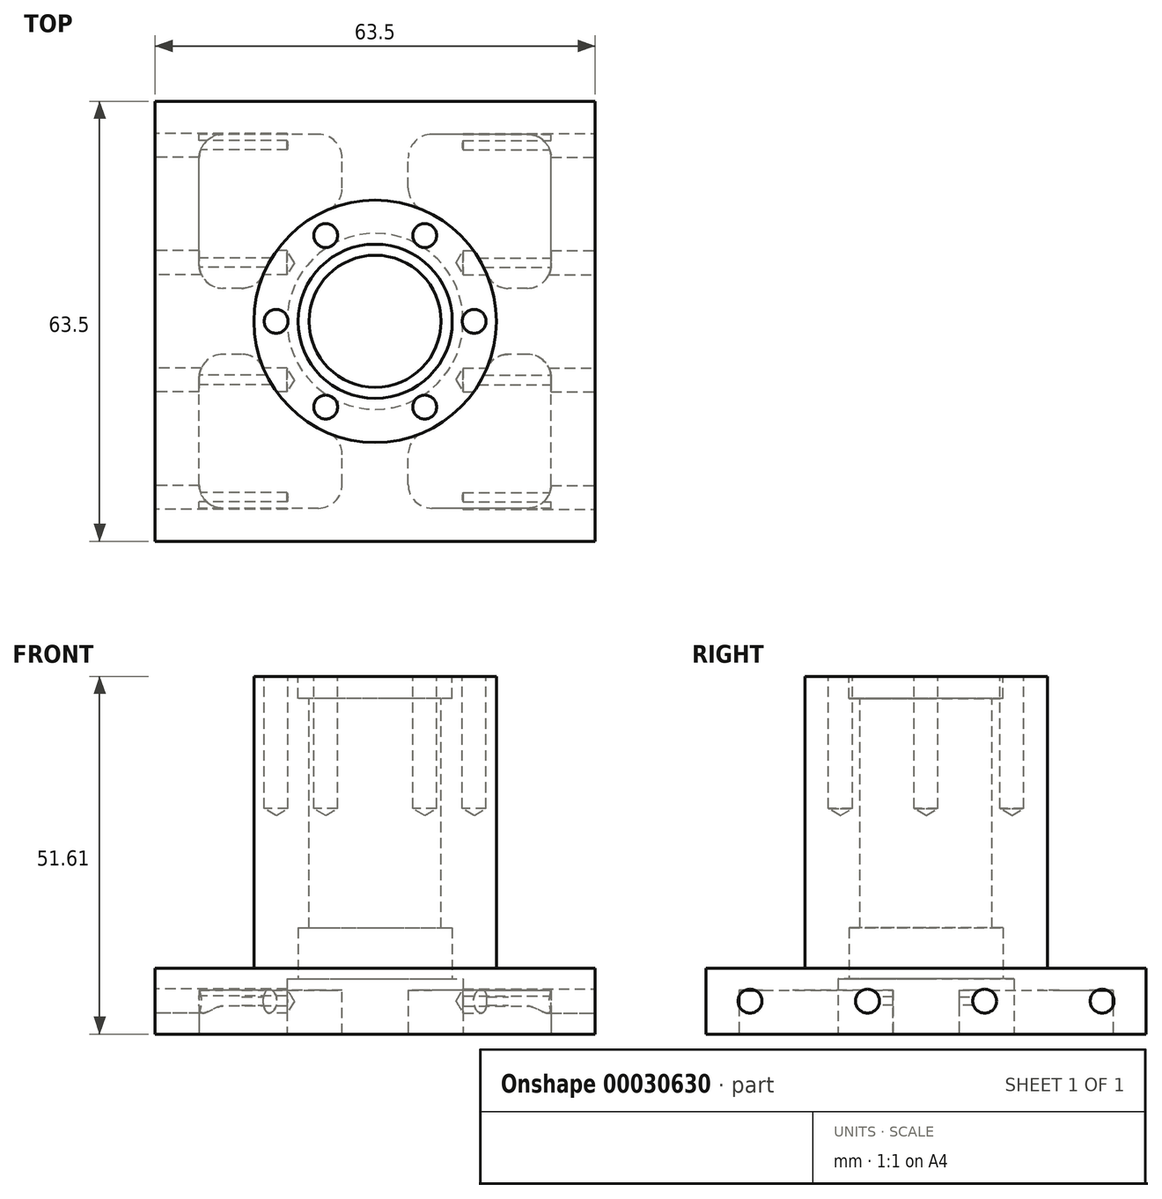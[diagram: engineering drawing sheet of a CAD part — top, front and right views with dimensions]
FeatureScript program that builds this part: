
annotation { "Feature Type Name" : "Feature", "Feature Type Description" : "" }
export const myFeature = defineFeature(function(context is Context, id is Id, definition is map)
    precondition{}
    {
        {
            var Q0;
            Q0=qCreatedBy(makeId("Top.planeOp"),FACE);
            var sketch = newSketch(context, id + "F0", { "sketchPlane" : qUnion([Q0])});
            skLineSegment(sketch, "E0.rect.bottom", {"start": v(31.75, -31.75) * mm, "end": v(-31.75, -31.75) * mm});
            skLineSegment(sketch, "E0.rect.top", {"start": v(31.75, 31.75) * mm, "end": v(-31.75, 31.75) * mm});
            skLineSegment(sketch, "E0.rect.left", {"start": v(31.75, -31.75) * mm, "end": v(31.75, 31.75) * mm});
            skLineSegment(sketch, "E0.rect.right", {"start": v(-31.75, -31.75) * mm, "end": v(-31.75, 31.75) * mm});
            skPoint(sketch, "E0.rect.middle", {"position": v(0, 0) * mm});
            skSolve(sketch);
        }
        {
            var Q0;
            Q0=makeQuery(id+"F0.imprint","IMPRINT",FACE,{"disambiguationData":[TD([[makeQuery(id+"F0.imprint","IMPRINT",EDGE,{"derivedFrom":sQuery(id+"F0.wireOp",EDGE,"E0.rect.bottom")}),-1.0]])]});
            extrude(context, id + "F1", {"entities" : qUnion([Q0]), "depth" : 9.52 * mm});
        }
        {
            var Q0;
            Q0=makeQuery(id+"F1.opExtrude","CAP_FACE",FACE,{"disambiguationData":[OSD([sQuery(id+"F0.wireOp",EDGE,"E0.rect.bottom"),sQuery(id+"F0.wireOp",EDGE,"E0.rect.top"),sQuery(id+"F0.wireOp",EDGE,"E0.rect.left"),sQuery(id+"F0.wireOp",EDGE,"E0.rect.right")])],"isStart":false});
            var sketch = newSketch(context, id + "F2", { "sketchPlane" : qUnion([Q0])});
            skCircle(sketch, "E1", {"center": v(0, 0) * mm, "radius": 17.49 * mm});
            skSolve(sketch);
        }
        {
            var Q0;
            Q0=makeQuery(id+"F2.imprint","IMPRINT",FACE,{"disambiguationData":[TD([[makeQuery(id+"F2.imprint","IMPRINT",EDGE,{"derivedFrom":sQuery(id+"F2.wireOp",EDGE,"E1")}),1.0]])]});
            extrude(context, id + "F3", {"entities" : qUnion([Q0]), "operationType" : NewBodyOperationType.ADD, "depth" : 42.1 * mm});
        }
        {
            var Q0;
            Q0=makeQuery(id+"F3.opExtrude","CAP_FACE",FACE,{"disambiguationData":[OSD([sQuery(id+"F2.wireOp",EDGE,"E1")])],"isStart":false});
            var sketch = newSketch(context, id + "F4", { "sketchPlane" : qUnion([Q0])});
            skCircle(sketch, "E2", {"center": v(0, 0) * mm, "radius": 9.53 * mm});
            skSolve(sketch);
        }
        {
            var Q0;
            Q0 = qSketchRegion(id + "F4", true);
            extrude(context, id + "F5", {"entities" : qUnion([Q0]), "operationType" : NewBodyOperationType.REMOVE, "endBound" : BoundingType.THROUGH_ALL, "oppositeDirection" : true, "depth" : 25.4 * mm});
        }
        {
            var Q0;
            Q0=makeQuery(id+"F3.opExtrude","CAP_FACE",FACE,{"disambiguationData":[OSD([sQuery(id+"F2.wireOp",EDGE,"E1")])],"isStart":false});
            var sketch = newSketch(context, id + "F6", { "sketchPlane" : qUnion([Q0])});
            skCircle(sketch, "E3", {"center": v(0, 0) * mm, "radius": 11.13 * mm});
            skSolve(sketch);
        }
        {
            var Q0;
            Q0=makeQuery(id+"F6.imprint","IMPRINT",FACE,{"disambiguationData":[TD([[makeQuery(id+"F6.imprint","IMPRINT",EDGE,{"derivedFrom":sQuery(id+"F6.wireOp",EDGE,"E3")}),1.0]])]});
            extrude(context, id + "F7", {"entities" : qUnion([Q0]), "operationType" : NewBodyOperationType.REMOVE, "oppositeDirection" : true, "depth" : 3.17 * mm});
        }
        {
            var Q0;
            Q0=makeQuery(id+"F1.opExtrude","CAP_FACE",FACE,{"disambiguationData":[OSD([sQuery(id+"F0.wireOp",EDGE,"E0.rect.bottom"),sQuery(id+"F0.wireOp",EDGE,"E0.rect.top"),sQuery(id+"F0.wireOp",EDGE,"E0.rect.left"),sQuery(id+"F0.wireOp",EDGE,"E0.rect.right")])],"isStart":true});
            var sketch = newSketch(context, id + "F8", { "sketchPlane" : qUnion([Q0])});
            skCircle(sketch, "E4", {"center": v(0, 0) * mm, "radius": 11.13 * mm});
            skSolve(sketch);
        }
        {
            var Q0;
            Q0 = qSketchRegion(id + "F8", true);
            extrude(context, id + "F9", {"entities" : qUnion([Q0]), "operationType" : NewBodyOperationType.REMOVE, "oppositeDirection" : true, "depth" : 15.32 * mm});
        }
        {
            var Q0;
            Q0=makeQuery(id+"F1.opExtrude","CAP_FACE",FACE,{"disambiguationData":[OSD([sQuery(id+"F0.wireOp",EDGE,"E0.rect.bottom"),sQuery(id+"F0.wireOp",EDGE,"E0.rect.top"),sQuery(id+"F0.wireOp",EDGE,"E0.rect.left"),sQuery(id+"F0.wireOp",EDGE,"E0.rect.right")])],"isStart":true});
            var sketch = newSketch(context, id + "F10", { "sketchPlane" : qUnion([Q0])});
            skCircle(sketch, "E5", {"center": v(0, 0) * mm, "radius": 12.7 * mm});
            skSolve(sketch);
        }
        {
            var Q0;
            Q0=makeQuery(id+"F10.imprint","IMPRINT",FACE,{"disambiguationData":[TD([[makeQuery(id+"F10.imprint","IMPRINT",EDGE,{"derivedFrom":sQuery(id+"F10.wireOp",EDGE,"E5")}),1.0]])]});
            var Q1;
            Q1=sQuery(id+"F10.wireOp",EDGE,"E5");
            extrude(context, id + "F11", {"entities" : qUnion([Q0]), "operationType" : NewBodyOperationType.REMOVE, "surfaceEntities" : qUnion([Q1]), "oppositeDirection" : true, "depth" : 7.95 * mm});
        }
        {
            var Q0;
            Q0=makeQuery(id+"F3.opExtrude","CAP_FACE",FACE,{"disambiguationData":[OSD([sQuery(id+"F2.wireOp",EDGE,"E1")])],"isStart":false});
            var sketch = newSketch(context, id + "F12", { "sketchPlane" : qUnion([Q0])});
            skCircle(sketch, "E6.cCircle", {"center": v(0, 0) * mm, "radius": 14.29 * mm, "construction": true});
            skLineSegment(sketch, "E6.0", {"start": v(-14.29, 0) * mm, "end": v(-7.14, 12.37) * mm});
            skLineSegment(sketch, "E6.1", {"start": v(-7.14, 12.37) * mm, "end": v(7.14, 12.37) * mm});
            skLineSegment(sketch, "E6.2", {"start": v(7.14, 12.37) * mm, "end": v(14.29, 0) * mm});
            skLineSegment(sketch, "E6.3", {"start": v(14.29, 0) * mm, "end": v(7.14, -12.37) * mm});
            skLineSegment(sketch, "E6.4", {"start": v(7.14, -12.37) * mm, "end": v(-7.14, -12.37) * mm});
            skLineSegment(sketch, "E6.5", {"start": v(-7.14, -12.37) * mm, "end": v(-14.29, 0) * mm});
            skSolve(sketch);
        }
        {
            var Q0;
            Q0=sQuery(id+"F12.wireOp",VERTEX,"E6.3.start");
            var Q1;
            Q1=sQuery(id+"F12.wireOp",VERTEX,"E6.4.start");
            var Q2;
            Q2=sQuery(id+"F12.wireOp",VERTEX,"E6.5.start");
            var Q3;
            Q3=sQuery(id+"F12.wireOp",VERTEX,"E6.5.end");
            var Q4;
            Q4=sQuery(id+"F12.wireOp",VERTEX,"E6.1.start");
            var Q5;
            Q5=sQuery(id+"F12.wireOp",VERTEX,"E6.2.start");
            var Q6;
            Q6=makeQuery(id+"F1.opExtrude","SWEPT_BODY",BODY,{"disambiguationData":[OSD([sQuery(id+"F0.wireOp",EDGE,"E0.rect.bottom"),sQuery(id+"F0.wireOp",EDGE,"E0.rect.top"),sQuery(id+"F0.wireOp",EDGE,"E0.rect.left"),sQuery(id+"F0.wireOp",EDGE,"E0.rect.right")])]});
            hole(context, id + "F13", {"style" : HoleStyle.SIMPLE, "holeDiameter" : 3.45 * mm, "endStyle" : HoleEndStyle.BLIND, "holeDepth" : 19.05 * mm, "locations" : qUnion([Q0, Q1, Q2, Q3, Q4, Q5]), "scope" : qUnion([Q6])});
        }
        {
            var Q0;
            Q0=makeQuery(id+"F1.opExtrude","SWEPT_FACE",FACE,{"disambiguationData":[OSD([sQuery(id+"F0.wireOp",EDGE,"E0.rect.left")])]});
            var sketch = newSketch(context, id + "F14", { "sketchPlane" : qUnion([Q0])});
            skLineSegment(sketch, "E7", {"start": v(31.75, 4.76) * mm, "end": v(-31.75, 4.76) * mm});
            skPoint(sketch, "E8", {"position": v(25.4, 4.76) * mm});
            skPoint(sketch, "E9", {"position": v(-25.4, 4.76) * mm});
            skPoint(sketch, "E10", {"position": v(-8.46, 4.76) * mm});
            skPoint(sketch, "E11", {"position": v(8.46, 4.76) * mm});
            skSolve(sketch);
        }
        {
            var Q0;
            Q0=sQuery(id+"F14.wireOp",VERTEX,"E8");
            var Q1;
            Q1=sQuery(id+"F14.wireOp",VERTEX,"E11");
            var Q2;
            Q2=sQuery(id+"F14.wireOp",VERTEX,"E10");
            var Q3;
            Q3=sQuery(id+"F14.wireOp",VERTEX,"E9");
            var Q4;
            Q4=makeQuery(id+"F1.opExtrude","SWEPT_BODY",BODY,{"disambiguationData":[OSD([sQuery(id+"F0.wireOp",EDGE,"E0.rect.bottom"),sQuery(id+"F0.wireOp",EDGE,"E0.rect.top"),sQuery(id+"F0.wireOp",EDGE,"E0.rect.left"),sQuery(id+"F0.wireOp",EDGE,"E0.rect.right")])]});
            hole(context, id + "F15", {"style" : HoleStyle.SIMPLE, "holeDiameter" : 3.45 * mm, "endStyle" : HoleEndStyle.BLIND, "holeDepth" : 19.05 * mm, "locations" : qUnion([Q0, Q1, Q2, Q3]), "scope" : qUnion([Q4])});
        }
        {
            var Q0;
            Q0=makeQuery(id+"F1.opExtrude","SWEPT_FACE",FACE,{"disambiguationData":[OSD([sQuery(id+"F0.wireOp",EDGE,"E0.rect.right")])]});
            var sketch = newSketch(context, id + "F16", { "sketchPlane" : qUnion([Q0])});
            skLineSegment(sketch, "E12", {"start": v(31.75, 4.76) * mm, "end": v(-31.75, 4.76) * mm});
            skPoint(sketch, "E13", {"position": v(25.4, 4.76) * mm});
            skPoint(sketch, "E14", {"position": v(8.46, 4.76) * mm});
            skPoint(sketch, "E15", {"position": v(-8.46, 4.76) * mm});
            skPoint(sketch, "E16", {"position": v(-25.4, 4.76) * mm});
            skSolve(sketch);
        }
        {
            var Q0;
            Q0=sQuery(id+"F16.wireOp",VERTEX,"E13");
            var Q1;
            Q1=sQuery(id+"F16.wireOp",VERTEX,"E14");
            var Q2;
            Q2=sQuery(id+"F16.wireOp",VERTEX,"E15");
            var Q3;
            Q3=sQuery(id+"F16.wireOp",VERTEX,"E16");
            var Q4;
            Q4=makeQuery(id+"F1.opExtrude","SWEPT_BODY",BODY,{"disambiguationData":[OSD([sQuery(id+"F0.wireOp",EDGE,"E0.rect.bottom"),sQuery(id+"F0.wireOp",EDGE,"E0.rect.top"),sQuery(id+"F0.wireOp",EDGE,"E0.rect.left"),sQuery(id+"F0.wireOp",EDGE,"E0.rect.right")])]});
            hole(context, id + "F17", {"style" : HoleStyle.SIMPLE, "holeDiameter" : 3.45 * mm, "endStyle" : HoleEndStyle.BLIND, "holeDepth" : 19.05 * mm, "locations" : qUnion([Q0, Q1, Q2, Q3]), "scope" : qUnion([Q4])});
        }
        {
            var Q0;
            Q0=makeQuery(id+"F1.opExtrude","CAP_FACE",FACE,{"disambiguationData":[OSD([sQuery(id+"F0.wireOp",EDGE,"E0.rect.bottom"),sQuery(id+"F0.wireOp",EDGE,"E0.rect.top"),sQuery(id+"F0.wireOp",EDGE,"E0.rect.left"),sQuery(id+"F0.wireOp",EDGE,"E0.rect.right")])],"isStart":true});
            var sketch = newSketch(context, id + "F18", { "sketchPlane" : qUnion([Q0])});
            skLineSegment(sketch, "E17.0", {"start": v(25.4, 26.97) * mm, "end": v(25.4, 4.76) * mm});
            skLineSegment(sketch, "E18.0", {"start": v(-25.4, 26.97) * mm, "end": v(-25.4, 4.76) * mm});
            skLineSegment(sketch, "E19.0", {"start": v(25.4, -26.97) * mm, "end": v(4.76, -26.97) * mm});
            skLineSegment(sketch, "E20.0", {"start": v(25.4, 26.97) * mm, "end": v(4.76, 26.97) * mm});
            skArc(sketch, "E21.0", {"start": v(-16.81, -4.76) * mm, "mid": v(-12.36, -12.36) * mm, "end": v(-4.76, -16.81) * mm});
            skLineSegment(sketch, "E22.rect.bottom", {"start": v(25.4, 4.76) * mm, "end": v(16.81, 4.76) * mm});
            skLineSegment(sketch, "E22.rect.top", {"start": v(25.4, -4.76) * mm, "end": v(16.81, -4.76) * mm});
            skLineSegment(sketch, "E23.rect.left", {"start": v(4.76, 26.97) * mm, "end": v(4.76, 16.81) * mm});
            skLineSegment(sketch, "E23.rect.right", {"start": v(-4.76, 26.97) * mm, "end": v(-4.76, 16.81) * mm});
            skPoint(sketch, "E22.rect.right.end.orphan", {"position": v(-36.4, -4.76) * mm});
            skPoint(sketch, "E24.orphan", {"position": v(-36.4, 4.76) * mm});
            skLineSegment(sketch, "E25.trimOffspring", {"start": v(-25.4, -4.76) * mm, "end": v(-25.4, -26.97) * mm});
            skPoint(sketch, "E23.rect.bottom.end.orphan", {"position": v(-4.76, 36.56) * mm});
            skPoint(sketch, "E23.rect.bottom.start.orphan", {"position": v(4.76, 36.56) * mm});
            skPoint(sketch, "E22.rect.left.start.orphan", {"position": v(36.4, 4.76) * mm});
            skPoint(sketch, "E26.orphan", {"position": v(36.4, -4.76) * mm});
            skPoint(sketch, "E23.rect.top.start.orphan", {"position": v(4.76, -36.56) * mm});
            skPoint(sketch, "E27.orphan", {"position": v(-4.76, -36.56) * mm});
            skLineSegment(sketch, "E28.trimOffspring", {"start": v(-4.76, -26.97) * mm, "end": v(-25.4, -26.97) * mm});
            skLineSegment(sketch, "E29.trimOffspring", {"start": v(25.4, -4.76) * mm, "end": v(25.4, -26.97) * mm});
            skLineSegment(sketch, "E30.trimOffspring", {"start": v(-4.76, 26.97) * mm, "end": v(-25.4, 26.97) * mm});
            skLineSegment(sketch, "E31.trimOffspring", {"start": v(-4.76, -16.81) * mm, "end": v(-4.76, -26.97) * mm});
            skLineSegment(sketch, "E32.trimOffspring", {"start": v(4.76, -16.81) * mm, "end": v(4.76, -26.97) * mm});
            skLineSegment(sketch, "E33.trimOffspring", {"start": v(-16.81, -4.76) * mm, "end": v(-25.4, -4.76) * mm});
            skLineSegment(sketch, "E34.trimOffspring", {"start": v(-16.81, 4.76) * mm, "end": v(-25.4, 4.76) * mm});
            skArc(sketch, "E35.trimOffspring", {"start": v(4.76, -16.81) * mm, "mid": v(12.36, -12.36) * mm, "end": v(16.81, -4.76) * mm});
            skArc(sketch, "E36.trimOffspring", {"start": v(16.81, 4.76) * mm, "mid": v(12.36, 12.36) * mm, "end": v(4.76, 16.81) * mm});
            skArc(sketch, "E37.trimOffspring", {"start": v(-4.76, 16.81) * mm, "mid": v(-12.36, 12.36) * mm, "end": v(-16.81, 4.76) * mm});
            skSolve(sketch);
        }
        {
            var Q0;
            Q0=makeQuery(id+"F18.imprint","IMPRINT",FACE,{"disambiguationData":[TD([[makeQuery(id+"F18.imprint","IMPRINT",EDGE,{"derivedFrom":sQuery(id+"F18.wireOp",EDGE,"E21.0")}),-1.0]])]});
            var Q1;
            Q1=makeQuery(id+"F18.imprint","IMPRINT",FACE,{"disambiguationData":[TD([[makeQuery(id+"F18.imprint","IMPRINT",EDGE,{"derivedFrom":sQuery(id+"F18.wireOp",EDGE,"E18.0")}),1.0]])]});
            var Q2;
            Q2=makeQuery(id+"F18.imprint","IMPRINT",FACE,{"disambiguationData":[TD([[makeQuery(id+"F18.imprint","IMPRINT",EDGE,{"derivedFrom":sQuery(id+"F18.wireOp",EDGE,"E17.0")}),-1.0]])]});
            var Q3;
            Q3=makeQuery(id+"F18.imprint","IMPRINT",FACE,{"disambiguationData":[TD([[makeQuery(id+"F18.imprint","IMPRINT",EDGE,{"derivedFrom":sQuery(id+"F18.wireOp",EDGE,"E19.0")}),-1.0]])]});
            extrude(context, id + "F19", {"entities" : qUnion([Q0, Q1, Q2, Q3]), "operationType" : NewBodyOperationType.REMOVE, "oppositeDirection" : true, "depth" : 6.35 * mm});
        }
        {
            var Q0;
            {var subQ0=sQuery(id+"F18.wireOp",EDGE,"E30.trimOffspring");var subQ1=sQuery(id+"F18.wireOp",EDGE,"E18.0");Q0=makeQuery(id+"F19.boolean.opBoolean","COPY",EDGE,{"disambiguationData":[TD([makeQuery(id+"F1.opExtrude","CAP_FACE",FACE,{"disambiguationData":[OSD([sQuery(id+"F0.wireOp",EDGE,"E0.rect.bottom"),sQuery(id+"F0.wireOp",EDGE,"E0.rect.top"),sQuery(id+"F0.wireOp",EDGE,"E0.rect.left"),sQuery(id+"F0.wireOp",EDGE,"E0.rect.right")])],"isStart":true})])],"derivedFrom":makeQuery(id+"F19.opExtrude","SWEPT_EDGE",EDGE,{"disambiguationData":[OSD([subQ1,subQ0])]})});}
            var Q1;
            Q1=makeQuery(id+"F19.boolean.opBoolean","COPY",EDGE,{"derivedFrom":makeQuery(id+"F19.opExtrude","SWEPT_EDGE",EDGE,{"disambiguationData":[OSD([sQuery(id+"F18.wireOp",EDGE,"E20.0"),sQuery(id+"F18.wireOp",EDGE,"E23.rect.left")])]})});
            var Q2;
            Q2=makeQuery(id+"F19.boolean.opBoolean","COPY",EDGE,{"derivedFrom":makeQuery(id+"F19.opExtrude","SWEPT_EDGE",EDGE,{"disambiguationData":[OSD([sQuery(id+"F18.wireOp",EDGE,"E25.trimOffspring"),sQuery(id+"F18.wireOp",EDGE,"E33.trimOffspring")])]})});
            var Q3;
            Q3=makeQuery(id+"F19.boolean.opBoolean","COPY",EDGE,{"derivedFrom":makeQuery(id+"F19.opExtrude","SWEPT_EDGE",EDGE,{"disambiguationData":[OSD([sQuery(id+"F18.wireOp",EDGE,"E32.trimOffspring"),sQuery(id+"F18.wireOp",EDGE,"E35.trimOffspring")])]})});
            var Q4;
            Q4=makeQuery(id+"F19.boolean.opBoolean","COPY",EDGE,{"derivedFrom":makeQuery(id+"F19.opExtrude","SWEPT_EDGE",EDGE,{"disambiguationData":[OSD([sQuery(id+"F18.wireOp",EDGE,"E22.rect.top"),sQuery(id+"F18.wireOp",EDGE,"E35.trimOffspring")])]})});
            var Q5;
            Q5=makeQuery(id+"F19.boolean.opBoolean","COPY",EDGE,{"derivedFrom":makeQuery(id+"F19.opExtrude","SWEPT_EDGE",EDGE,{"disambiguationData":[OSD([sQuery(id+"F18.wireOp",EDGE,"E18.0"),sQuery(id+"F18.wireOp",EDGE,"E34.trimOffspring")])]})});
            var Q6;
            {var subQ0=sQuery(id+"F18.wireOp",EDGE,"E25.trimOffspring");var subQ1=sQuery(id+"F18.wireOp",EDGE,"E28.trimOffspring");Q6=makeQuery(id+"F19.boolean.opBoolean","COPY",EDGE,{"disambiguationData":[TD([makeQuery(id+"F1.opExtrude","CAP_FACE",FACE,{"disambiguationData":[OSD([sQuery(id+"F0.wireOp",EDGE,"E0.rect.bottom"),sQuery(id+"F0.wireOp",EDGE,"E0.rect.top"),sQuery(id+"F0.wireOp",EDGE,"E0.rect.left"),sQuery(id+"F0.wireOp",EDGE,"E0.rect.right")])],"isStart":true})])],"derivedFrom":makeQuery(id+"F19.opExtrude","SWEPT_EDGE",EDGE,{"disambiguationData":[OSD([subQ0,subQ1])]})});}
            var Q7;
            Q7=makeQuery(id+"F19.boolean.opBoolean","COPY",EDGE,{"derivedFrom":makeQuery(id+"F19.opExtrude","SWEPT_EDGE",EDGE,{"disambiguationData":[OSD([sQuery(id+"F18.wireOp",EDGE,"E19.0"),sQuery(id+"F18.wireOp",EDGE,"E32.trimOffspring")])]})});
            var Q8;
            Q8=makeQuery(id+"F19.boolean.opBoolean","COPY",EDGE,{"derivedFrom":makeQuery(id+"F19.opExtrude","SWEPT_EDGE",EDGE,{"disambiguationData":[OSD([sQuery(id+"F18.wireOp",EDGE,"E22.rect.bottom"),sQuery(id+"F18.wireOp",EDGE,"E36.trimOffspring")])]})});
            var Q9;
            Q9=makeQuery(id+"F19.boolean.opBoolean","COPY",EDGE,{"derivedFrom":makeQuery(id+"F19.opExtrude","SWEPT_EDGE",EDGE,{"disambiguationData":[OSD([sQuery(id+"F18.wireOp",EDGE,"E23.rect.left"),sQuery(id+"F18.wireOp",EDGE,"E36.trimOffspring")])]})});
            var Q10;
            Q10=makeQuery(id+"F19.boolean.opBoolean","COPY",EDGE,{"derivedFrom":makeQuery(id+"F19.opExtrude","SWEPT_EDGE",EDGE,{"disambiguationData":[OSD([sQuery(id+"F18.wireOp",EDGE,"E21.0"),sQuery(id+"F18.wireOp",EDGE,"E33.trimOffspring")])]})});
            var Q11;
            Q11=makeQuery(id+"F19.boolean.opBoolean","COPY",EDGE,{"derivedFrom":makeQuery(id+"F19.opExtrude","SWEPT_EDGE",EDGE,{"disambiguationData":[OSD([sQuery(id+"F18.wireOp",EDGE,"E21.0"),sQuery(id+"F18.wireOp",EDGE,"E31.trimOffspring")])]})});
            var Q12;
            Q12=makeQuery(id+"F19.boolean.opBoolean","COPY",EDGE,{"derivedFrom":makeQuery(id+"F19.opExtrude","SWEPT_EDGE",EDGE,{"disambiguationData":[OSD([sQuery(id+"F18.wireOp",EDGE,"E23.rect.right"),sQuery(id+"F18.wireOp",EDGE,"E30.trimOffspring")])]})});
            var Q13;
            {var subQ0=sQuery(id+"F18.wireOp",EDGE,"E17.0");var subQ1=sQuery(id+"F18.wireOp",EDGE,"E20.0");Q13=makeQuery(id+"F19.boolean.opBoolean","COPY",EDGE,{"disambiguationData":[TD([makeQuery(id+"F1.opExtrude","CAP_FACE",FACE,{"disambiguationData":[OSD([sQuery(id+"F0.wireOp",EDGE,"E0.rect.bottom"),sQuery(id+"F0.wireOp",EDGE,"E0.rect.top"),sQuery(id+"F0.wireOp",EDGE,"E0.rect.left"),sQuery(id+"F0.wireOp",EDGE,"E0.rect.right")])],"isStart":true})])],"derivedFrom":makeQuery(id+"F19.opExtrude","SWEPT_EDGE",EDGE,{"disambiguationData":[OSD([subQ0,subQ1])]})});}
            var Q14;
            Q14=makeQuery(id+"F19.boolean.opBoolean","COPY",EDGE,{"derivedFrom":makeQuery(id+"F19.opExtrude","SWEPT_EDGE",EDGE,{"disambiguationData":[OSD([sQuery(id+"F18.wireOp",EDGE,"E22.rect.top"),sQuery(id+"F18.wireOp",EDGE,"E29.trimOffspring")])]})});
            var Q15;
            Q15=makeQuery(id+"F19.boolean.opBoolean","COPY",EDGE,{"derivedFrom":makeQuery(id+"F19.opExtrude","SWEPT_EDGE",EDGE,{"disambiguationData":[OSD([sQuery(id+"F18.wireOp",EDGE,"E17.0"),sQuery(id+"F18.wireOp",EDGE,"E22.rect.bottom")])]})});
            var Q16;
            {var subQ0=sQuery(id+"F18.wireOp",EDGE,"E29.trimOffspring");var subQ1=sQuery(id+"F18.wireOp",EDGE,"E19.0");Q16=makeQuery(id+"F19.boolean.opBoolean","COPY",EDGE,{"disambiguationData":[TD([makeQuery(id+"F1.opExtrude","CAP_FACE",FACE,{"disambiguationData":[OSD([sQuery(id+"F0.wireOp",EDGE,"E0.rect.bottom"),sQuery(id+"F0.wireOp",EDGE,"E0.rect.top"),sQuery(id+"F0.wireOp",EDGE,"E0.rect.left"),sQuery(id+"F0.wireOp",EDGE,"E0.rect.right")])],"isStart":true})])],"derivedFrom":makeQuery(id+"F19.opExtrude","SWEPT_EDGE",EDGE,{"disambiguationData":[OSD([subQ1,subQ0])]})});}
            var Q17;
            Q17=makeQuery(id+"F19.boolean.opBoolean","COPY",EDGE,{"derivedFrom":makeQuery(id+"F19.opExtrude","SWEPT_EDGE",EDGE,{"disambiguationData":[OSD([sQuery(id+"F18.wireOp",EDGE,"E28.trimOffspring"),sQuery(id+"F18.wireOp",EDGE,"E31.trimOffspring")])]})});
            var Q18;
            Q18=makeQuery(id+"F19.boolean.opBoolean","COPY",EDGE,{"derivedFrom":makeQuery(id+"F19.opExtrude","SWEPT_EDGE",EDGE,{"disambiguationData":[OSD([sQuery(id+"F18.wireOp",EDGE,"E34.trimOffspring"),sQuery(id+"F18.wireOp",EDGE,"E37.trimOffspring")])]})});
            var Q19;
            Q19=makeQuery(id+"F19.boolean.opBoolean","COPY",EDGE,{"derivedFrom":makeQuery(id+"F19.opExtrude","SWEPT_EDGE",EDGE,{"disambiguationData":[OSD([sQuery(id+"F18.wireOp",EDGE,"E23.rect.right"),sQuery(id+"F18.wireOp",EDGE,"E37.trimOffspring")])]})});
            fillet(context, id + "F20", {"entities" : qUnion([Q0, Q1, Q2, Q3, Q4, Q5, Q6, Q7, Q8, Q9, Q10, Q11, Q12, Q13, Q14, Q15, Q16, Q17, Q18, Q19]), "radius" : 3.43 * mm, "tangentPropagation" : true, "allowEdgeOverflow" : false});
        }
    });
